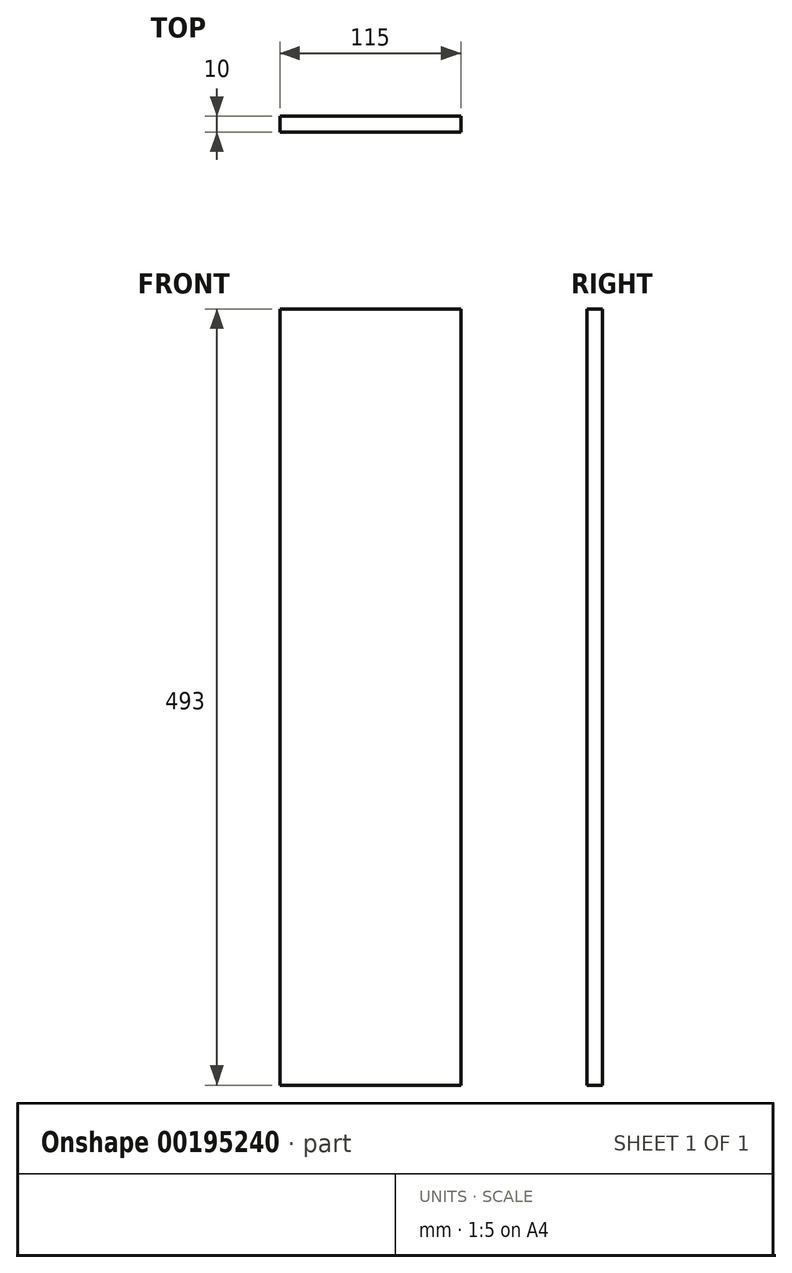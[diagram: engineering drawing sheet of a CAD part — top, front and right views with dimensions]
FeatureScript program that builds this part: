
annotation { "Feature Type Name" : "Feature", "Feature Type Description" : "" }
export const myFeature = defineFeature(function(context is Context, id is Id, definition is map)
    precondition{}
    {
        {
            var Q0;
            Q0=qCreatedBy(makeId("Front.planeOp"),FACE);
            var sketch = newSketch(context, id + "F0", { "sketchPlane" : qUnion([Q0])});
            skLineSegment(sketch, "E0.bottom", {"start": v(-57.5, 246.5) * mm, "end": v(57.5, 246.5) * mm});
            skLineSegment(sketch, "E0.top", {"start": v(-57.5, -246.5) * mm, "end": v(57.5, -246.5) * mm});
            skLineSegment(sketch, "E0.left", {"start": v(-57.5, 246.5) * mm, "end": v(-57.5, -246.5) * mm});
            skLineSegment(sketch, "E0.right", {"start": v(57.5, 246.5) * mm, "end": v(57.5, -246.5) * mm});
            skPoint(sketch, "E0.middle", {"position": v(0, 0) * mm});
            skSolve(sketch);
        }
        {
            var Q0;
            Q0=makeQuery(id+"F0.imprint","IMPRINT",FACE,{"disambiguationData":[TD([[makeQuery(id+"F0.imprint","IMPRINT",EDGE,{"derivedFrom":sQuery(id+"F0.wireOp",EDGE,"E0.bottom")}),-1.0]])]});
            extrude(context, id + "F1", {"entities" : qUnion([Q0]), "depth" : 10 * mm});
        }
    });
